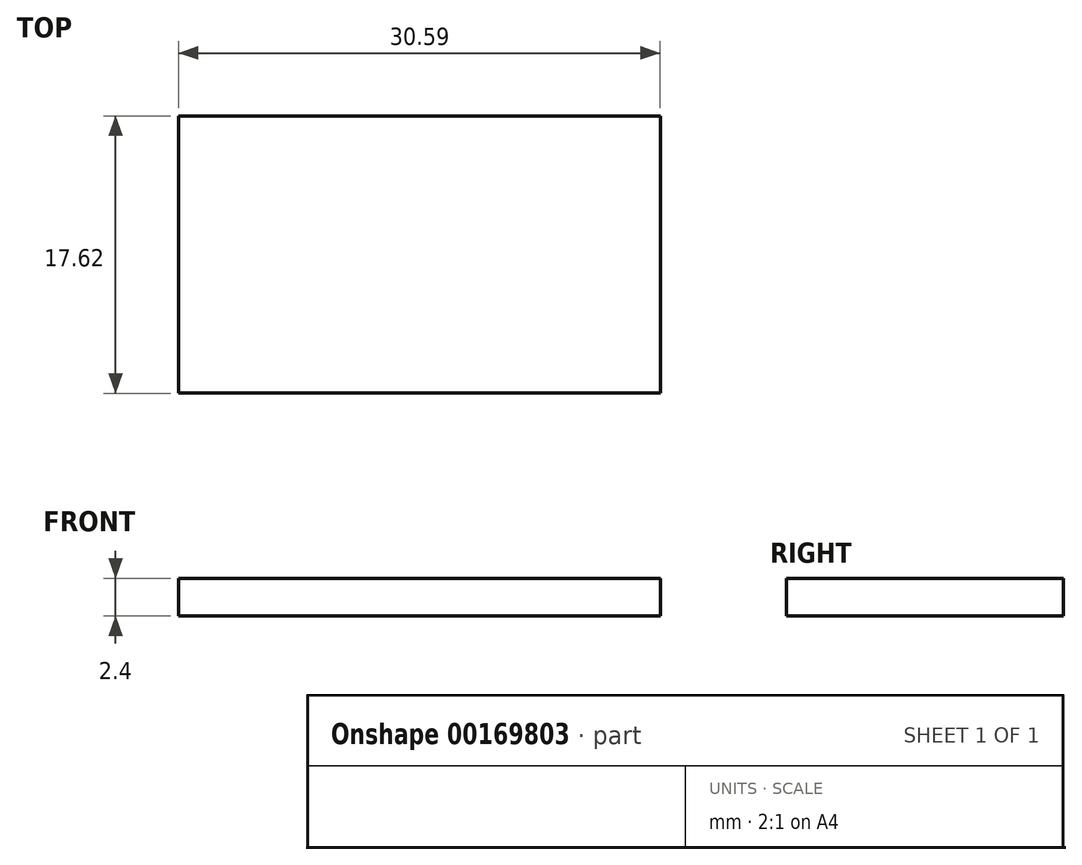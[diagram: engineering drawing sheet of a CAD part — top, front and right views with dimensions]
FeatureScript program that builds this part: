
annotation { "Feature Type Name" : "Feature", "Feature Type Description" : "" }
export const myFeature = defineFeature(function(context is Context, id is Id, definition is map)
    precondition{}
    {
        {
            var Q0;
            Q0=qCreatedBy(makeId("Top.planeOp"),FACE);
            var sketch = newSketch(context, id + "F0", { "sketchPlane" : qUnion([Q0])});
            skLineSegment(sketch, "E0.bottom", {"start": v(-28.05, 12.09) * mm, "end": v(2.54, 12.09) * mm});
            skLineSegment(sketch, "E0.top", {"start": v(-28.05, -5.53) * mm, "end": v(2.54, -5.53) * mm});
            skLineSegment(sketch, "E0.left", {"start": v(-28.05, 12.09) * mm, "end": v(-28.05, -5.53) * mm});
            skLineSegment(sketch, "E0.right", {"start": v(2.54, 12.09) * mm, "end": v(2.54, -5.53) * mm});
            skLineSegment(sketch, "E1.bottom", {"start": v(2.54, -5.53) * mm, "end": v(18.15, -5.53) * mm});
            skLineSegment(sketch, "E1.top", {"start": v(2.54, -15.83) * mm, "end": v(18.15, -15.83) * mm});
            skLineSegment(sketch, "E1.left", {"start": v(2.54, -5.53) * mm, "end": v(2.54, -15.83) * mm});
            skLineSegment(sketch, "E1.right", {"start": v(18.15, -5.53) * mm, "end": v(18.15, -15.83) * mm});
            skSolve(sketch);
        }
        {
            var Q0;
            Q0=makeQuery(id+"F0.imprint","IMPRINT",FACE,{"disambiguationData":[TD([[makeQuery(id+"F0.imprint","IMPRINT",EDGE,{"derivedFrom":sQuery(id+"F0.wireOp",EDGE,"E0.bottom")}),-1.0]])]});
            extrude(context, id + "F1", {"entities" : qUnion([Q0]), "depth" : 2.4 * mm});
        }
    });
